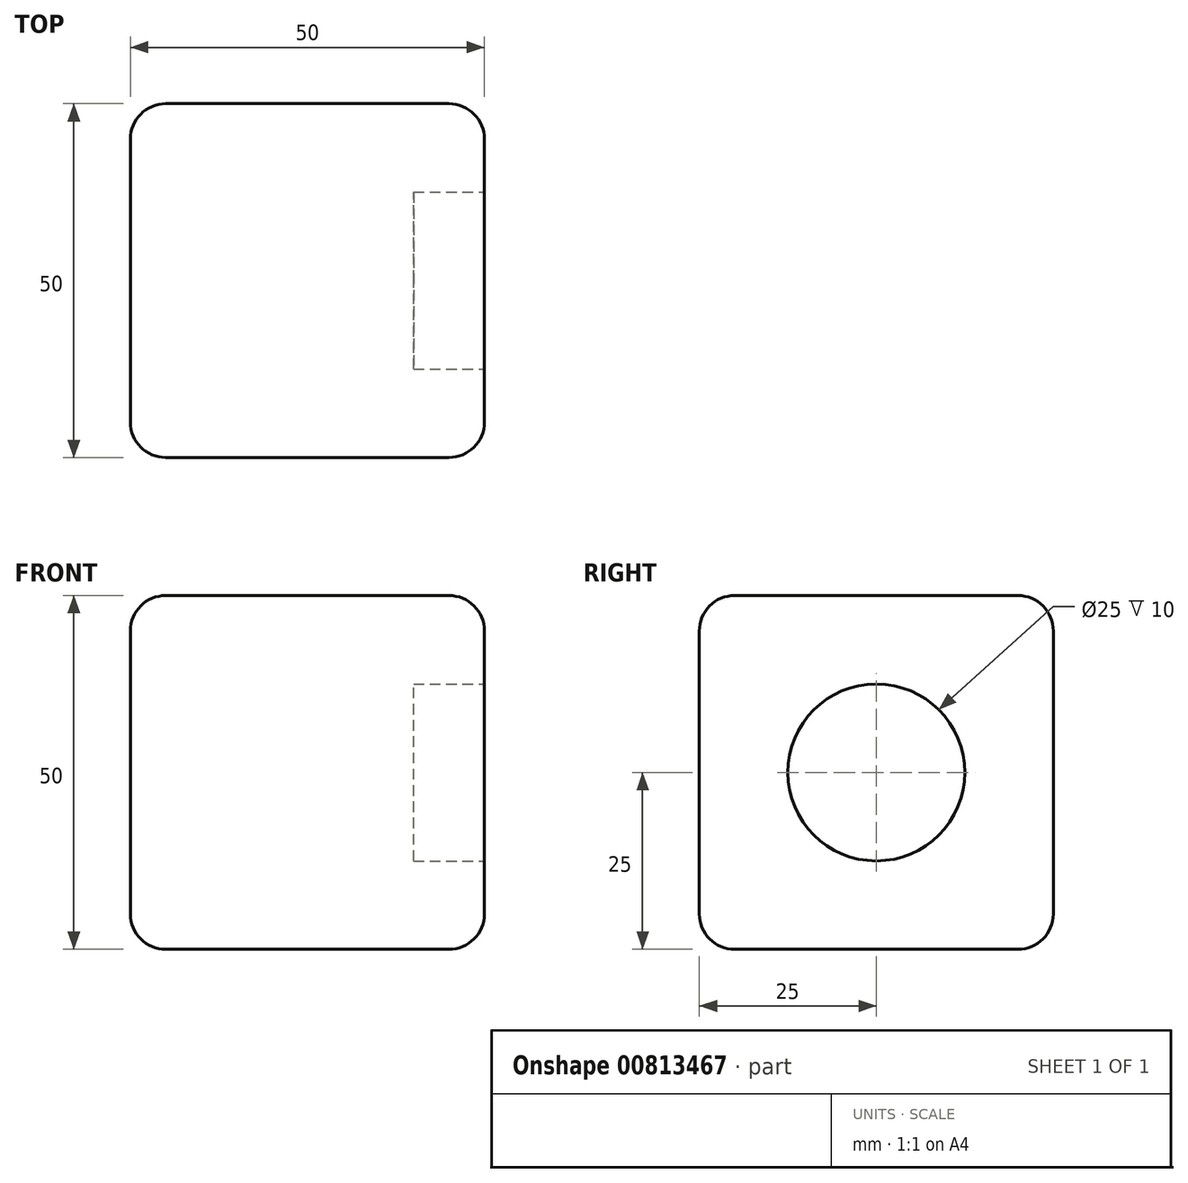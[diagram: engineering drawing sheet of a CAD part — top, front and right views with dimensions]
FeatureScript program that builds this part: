
annotation { "Feature Type Name" : "Feature", "Feature Type Description" : "" }
export const myFeature = defineFeature(function(context is Context, id is Id, definition is map)
    precondition{}
    {
        {
            var Q0;
            Q0=qCreatedBy(makeId("Top.planeOp"),FACE);
            var sketch = newSketch(context, id + "F0", { "sketchPlane" : qUnion([Q0])});
            skLineSegment(sketch, "E0.bottom", {"start": v(25, -25) * mm, "end": v(-25, -25) * mm});
            skLineSegment(sketch, "E0.top", {"start": v(25, 25) * mm, "end": v(-25, 25) * mm});
            skLineSegment(sketch, "E0.left", {"start": v(25, -25) * mm, "end": v(25, 25) * mm});
            skLineSegment(sketch, "E0.right", {"start": v(-25, -25) * mm, "end": v(-25, 25) * mm});
            skPoint(sketch, "E0.middle", {"position": v(0, 0) * mm});
            skSolve(sketch);
        }
        {
            var Q0;
            Q0 = qSketchRegion(id + "F0", true);
            extrude(context, id + "F1", {"entities" : qUnion([Q0]), "depth" : 50 * mm, "offsetDistance" : 25 * mm});
        }
        {
            var Q0;
            Q0=makeQuery(id+"F1.opExtrude","SWEPT_FACE",FACE,{"disambiguationData":[OSD([sQuery(id+"F0.wireOp",EDGE,"E0.left")])]});
            var sketch = newSketch(context, id + "F2", { "sketchPlane" : qUnion([Q0])});
            skLineSegment(sketch, "E1", {"start": v(0, 50) * mm, "end": v(0, 0) * mm, "construction": true});
            skCircle(sketch, "E2", {"center": v(0, 25) * mm, "radius": 12.5 * mm});
            skSolve(sketch);
        }
        {
            var Q0;
            Q0=makeQuery(id+"F2.imprint","IMPRINT",FACE,{"disambiguationData":[TD([[makeQuery(id+"F2.imprint","IMPRINT",EDGE,{"derivedFrom":sQuery(id+"F2.wireOp",EDGE,"E2")}),1.0]])]});
            extrude(context, id + "F3", {"entities" : qUnion([Q0]), "operationType" : NewBodyOperationType.REMOVE, "oppositeDirection" : true, "depth" : 10 * mm, "offsetDistance" : 25 * mm});
        }
        {
            var Q0;
            Q0=makeQuery(id+"F1.opExtrude","CAP_EDGE",EDGE,{"disambiguationData":[OSD([sQuery(id+"F0.wireOp",EDGE,"E0.left")])],"isStart":true});
            var Q1;
            Q1=makeQuery(id+"F1.opExtrude","SWEPT_EDGE",EDGE,{"disambiguationData":[OSD([sQuery(id+"F0.wireOp",EDGE,"E0.top"),sQuery(id+"F0.wireOp",EDGE,"E0.left")])]});
            var Q2;
            Q2=makeQuery(id+"F1.opExtrude","CAP_EDGE",EDGE,{"disambiguationData":[OSD([sQuery(id+"F0.wireOp",EDGE,"E0.left")])],"isStart":false});
            var Q3;
            Q3=makeQuery(id+"F1.opExtrude","SWEPT_EDGE",EDGE,{"disambiguationData":[OSD([sQuery(id+"F0.wireOp",EDGE,"E0.bottom"),sQuery(id+"F0.wireOp",EDGE,"E0.left")])]});
            var Q4;
            Q4=makeQuery(id+"F1.opExtrude","CAP_EDGE",EDGE,{"disambiguationData":[OSD([sQuery(id+"F0.wireOp",EDGE,"E0.top")])],"isStart":true});
            var Q5;
            Q5=makeQuery(id+"F1.opExtrude","CAP_EDGE",EDGE,{"disambiguationData":[OSD([sQuery(id+"F0.wireOp",EDGE,"E0.bottom")])],"isStart":true});
            var Q6;
            Q6=makeQuery(id+"F1.opExtrude","CAP_EDGE",EDGE,{"disambiguationData":[OSD([sQuery(id+"F0.wireOp",EDGE,"E0.bottom")])],"isStart":false});
            var Q7;
            Q7=makeQuery(id+"F1.opExtrude","CAP_EDGE",EDGE,{"disambiguationData":[OSD([sQuery(id+"F0.wireOp",EDGE,"E0.top")])],"isStart":false});
            var Q8;
            Q8=makeQuery(id+"F1.opExtrude","SWEPT_EDGE",EDGE,{"disambiguationData":[OSD([sQuery(id+"F0.wireOp",EDGE,"E0.top"),sQuery(id+"F0.wireOp",EDGE,"E0.right")])]});
            var Q9;
            Q9=makeQuery(id+"F1.opExtrude","CAP_EDGE",EDGE,{"disambiguationData":[OSD([sQuery(id+"F0.wireOp",EDGE,"E0.right")])],"isStart":true});
            var Q10;
            Q10=makeQuery(id+"F1.opExtrude","CAP_EDGE",EDGE,{"disambiguationData":[OSD([sQuery(id+"F0.wireOp",EDGE,"E0.right")])],"isStart":false});
            var Q11;
            Q11=makeQuery(id+"F1.opExtrude","SWEPT_EDGE",EDGE,{"disambiguationData":[OSD([sQuery(id+"F0.wireOp",EDGE,"E0.bottom"),sQuery(id+"F0.wireOp",EDGE,"E0.right")])]});
            fillet(context, id + "F4", {"entities" : qUnion([Q0, Q1, Q2, Q3, Q4, Q5, Q6, Q7, Q8, Q9, Q10, Q11]), "radius" : 5 * mm, "tangentPropagation" : true, "allowEdgeOverflow" : false});
        }
    });
